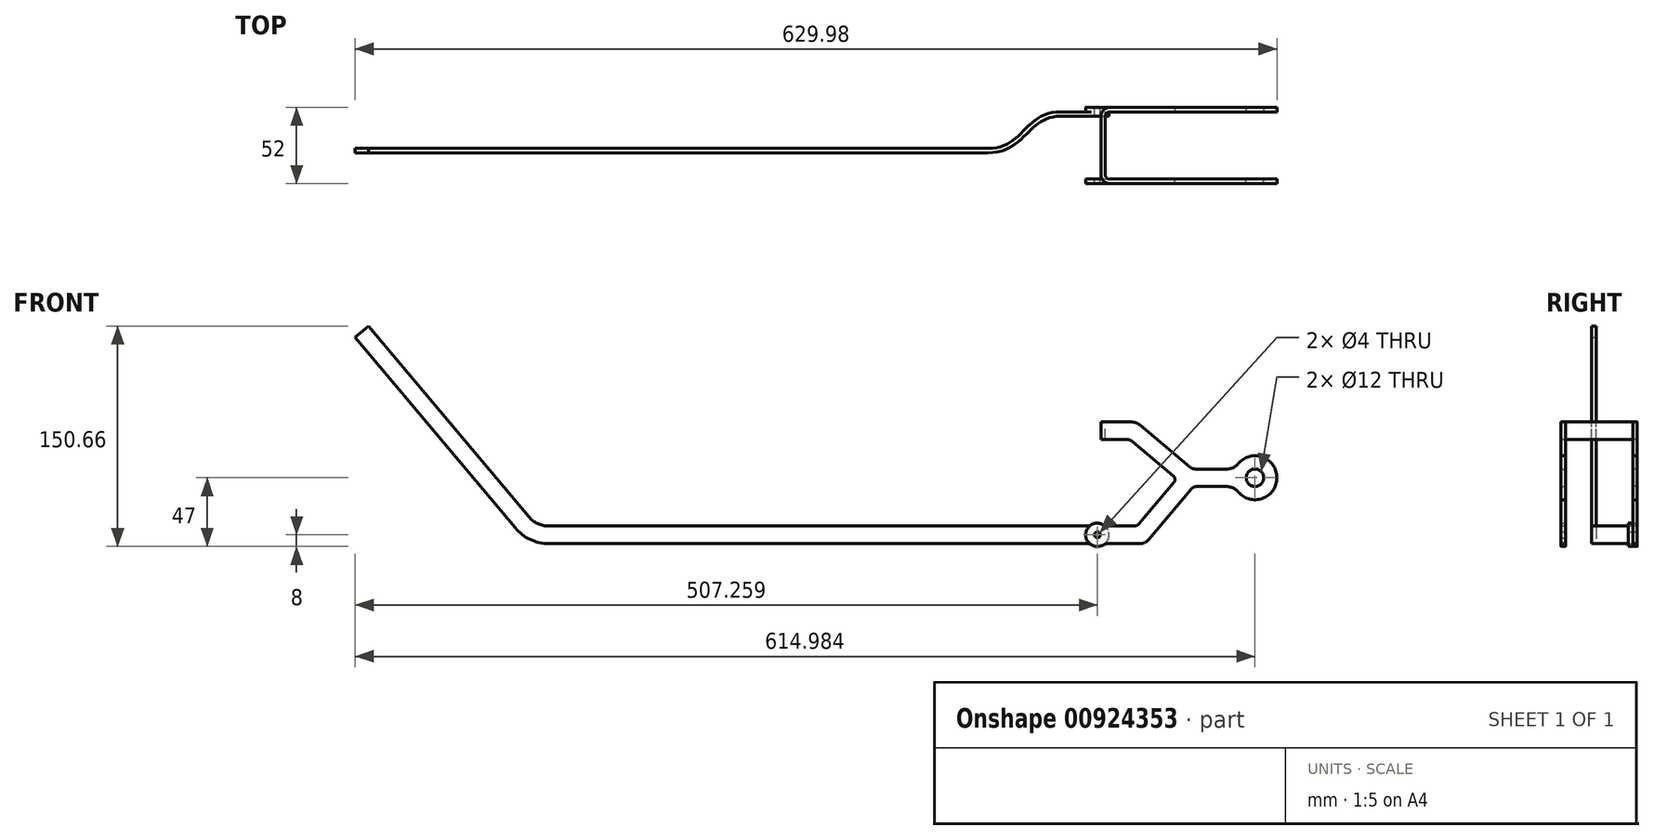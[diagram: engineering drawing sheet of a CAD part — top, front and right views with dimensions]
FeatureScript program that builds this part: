
annotation { "Feature Type Name" : "Feature", "Feature Type Description" : "" }
export const myFeature = defineFeature(function(context is Context, id is Id, definition is map)
    precondition{}
    {
        {
            var Q0;
            Q0=qCreatedBy(makeId("Front.planeOp"),FACE);
            var sketch = newSketch(context, id + "F0", { "sketchPlane" : qUnion([Q0])});
            skLineSegment(sketch, "E0", {"start": v(13.99, 0) * mm, "end": v(313.99, 0) * mm});
            skLineSegment(sketch, "E1", {"start": v(-9, 10.72) * mm, "end": v(-118.27, 140.94) * mm});
            skLineSegment(sketch, "E2", {"start": v(-23.81, 6) * mm, "end": v(-4.01, 6) * mm, "construction": true});
            skPoint(sketch, "E3.visualSharp", {"position": v(0, 0) * mm});
            skArc(sketch, "E3.filletArc", {"start": v(-9, 10.72) * mm, "mid": v(1.31, 2.81) * mm, "end": v(13.99, 0) * mm});
            skLineSegment(sketch, "E4.0", {"start": v(13.99, 12) * mm, "end": v(313.99, 12) * mm});
            skArc(sketch, "E4.1", {"start": v(0.2, 18.43) * mm, "mid": v(6.38, 13.69) * mm, "end": v(13.99, 12) * mm});
            skLineSegment(sketch, "E4.2", {"start": v(0.2, 18.43) * mm, "end": v(-109.07, 148.66) * mm});
            skLineSegment(sketch, "E5", {"start": v(-109.07, 148.66) * mm, "end": v(-118.27, 140.94) * mm});
            skLineSegment(sketch, "E6", {"start": v(313.99, 12) * mm, "end": v(313.99, 0) * mm});
            skSolve(sketch);
        }
        {
            var Q0;
            Q0=makeQuery(id+"F0.imprint","IMPRINT",FACE,{"disambiguationData":[TD([[makeQuery(id+"F0.imprint","IMPRINT",EDGE,{"derivedFrom":sQuery(id+"F0.wireOp",EDGE,"E0")}),1.0]])]});
            extrude(context, id + "F1", {"entities" : qUnion([Q0]), "depth" : 3 * mm, "offsetDistance" : 25 * mm});
        }
        {
            var Q0;
            Q0=qCreatedBy(makeId("Top.planeOp"),FACE);
            var sketch = newSketch(context, id + "F2", { "sketchPlane" : qUnion([Q0])});
            skLineSegment(sketch, "E7.0", {"start": v(13.99, 0) * mm, "end": v(313.99, 0) * mm});
            skSolve(sketch);
        }
        {
            var Q0;
            Q0=makeQuery(id+"F1.opExtrude","CAP_FACE",FACE,{"disambiguationData":[OSD([sQuery(id+"F0.wireOp",EDGE,"E0"),sQuery(id+"F0.wireOp",EDGE,"E1"),sQuery(id+"F0.wireOp",EDGE,"E3.filletArc"),sQuery(id+"F0.wireOp",EDGE,"E4.0"),sQuery(id+"F0.wireOp",EDGE,"E4.1"),sQuery(id+"F0.wireOp",EDGE,"E4.2"),sQuery(id+"F0.wireOp",EDGE,"E5"),sQuery(id+"F0.wireOp",EDGE,"E6")])],"isStart":true});
            cPlane(context, id + "F3", {"entities" : qUnion([Q0]), "cplaneType" : CPlaneType.OFFSET, "offset" : 25 * mm, "width" : 150 * mm, "height" : 150 * mm});
        }
        {
            var Q0;
            Q0=makeQuery(id+"F1.opExtrude","SWEPT_FACE",FACE,{"disambiguationData":[OSD([sQuery(id+"F0.wireOp",EDGE,"E0")])]});
            var sketch = newSketch(context, id + "F4", { "sketchPlane" : qUnion([Q0])});
            skPoint(sketch, "E8.0", {"position": v(313.99, 0) * mm});
            skFitSpline(sketch, "E9", {"points": [v(313.99, 0) * mm, v(363.99, -25) * mm], "startDerivative": vector(75, 0) * mm, "endDerivative": vector(75, 0) * mm});
            skLineSegment(sketch, "E10", {"start": v(363.99, -25) * mm, "end": v(388.99, -25) * mm});
            skLineSegment(sketch, "E11", {"start": v(363.99, -25) * mm, "end": v(241.15, -25) * mm, "construction": true});
            skSolve(sketch);
        }
        {
            var Q0;
            Q0=makeQuery(id+"F1.opExtrude","SWEPT_FACE",FACE,{"disambiguationData":[OSD([sQuery(id+"F0.wireOp",EDGE,"E6")])]});
            var Q1;
            Q1=sQuery(id+"F4.wireOp",EDGE,"E9");
            var Q2;
            Q2=sQuery(id+"F4.wireOp",EDGE,"E10");
            sweep(context, id + "F5", {"operationType" : NewBodyOperationType.ADD, "profiles" : qUnion([Q0]), "path" : qUnion([Q1, Q2])});
        }
        {
            var Q0;
            {var subQ0=sQuery(id+"F4.wireOp",EDGE,"E10");var subQ1=sQuery(id+"F0.wireOp",EDGE,"E6");Q0=makeQuery(id+"F5.opSweep","SWEPT_FACE",FACE,{"disambiguationData":[OSD([subQ1,subQ0]),TDD([makeQuery(id+"F1.opExtrude","CAP_EDGE",EDGE,{"disambiguationData":[OSD([subQ1])],"isStart":true}),subQ0])]});}
            var sketch = newSketch(context, id + "F6", { "sketchPlane" : qUnion([Q0])});
            skCircle(sketch, "E12", {"center": v(-388.99, 6) * mm, "radius": 6 * mm});
            skCircle(sketch, "E13", {"center": v(-388.99, 6) * mm, "radius": 2 * mm});
            skCircle(sketch, "E14", {"center": v(-388.99, 6) * mm, "radius": 8 * mm});
            skSolve(sketch);
        }
        {
            var Q0;
            {var subQ2=sQuery(id+"F0.wireOp",EDGE,"E6");var subQ4=sQuery(id+"F4.wireOp",EDGE,"E10");var subQ5=sQuery(id+"F0.wireOp",EDGE,"E0");var subQ6=makeQuery(id+"F5.opSweep","SWEPT_EDGE",EDGE,{"disambiguationData":[OSD([subQ5,subQ2,subQ4]),TDD([makeQuery(id+"F1.opExtrude","CAP_VERTEX",VERTEX,{"disambiguationData":[OSD([subQ5,subQ2])],"isStart":true}),subQ4])]});var subQ11=sQuery(id+"F6.wireOp",EDGE,"E14");var subQ13=makeQuery(id+"F6.imprint","INTERSECT",VERTEX,{"derivedFrom":[subQ6,subQ11]});Q0=makeQuery(id+"F6.imprint","IMPRINT",FACE,{"disambiguationData":[TD([[makeQuery(id+"F6.imprint","IMPRINT",EDGE,{"disambiguationData":[TD([[subQ13,1.0]])],"derivedFrom":subQ11}),1.0]])]});}
            var Q1;
            {var subQ1=sQuery(id+"F4.wireOp",VERTEX,"E10.end");var subQ2=sQuery(id+"F0.wireOp",EDGE,"E6");var subQ3=makeQuery(id+"F5.opSweep","CAP_EDGE",EDGE,{"disambiguationData":[OSD([subQ2,subQ1]),TDD([makeQuery(id+"F1.opExtrude","CAP_EDGE",EDGE,{"disambiguationData":[OSD([subQ2])],"isStart":true}),subQ1])],"isStart":false});var subQ9=sQuery(id+"F6.wireOp",EDGE,"E13");var subQ10=makeQuery(id+"F6.imprint","INTERSECT",VERTEX,{"disambiguationData":[OD(0.0)],"derivedFrom":[subQ3,subQ9]});Q1=makeQuery(id+"F6.imprint","IMPRINT",FACE,{"disambiguationData":[TD([[makeQuery(id+"F6.imprint","IMPRINT",EDGE,{"disambiguationData":[TD([[subQ10,1.0]])],"derivedFrom":subQ9}),-1.0]])]});}
            var Q2;
            {var subQ1=sQuery(id+"F4.wireOp",VERTEX,"E10.end");var subQ2=sQuery(id+"F0.wireOp",EDGE,"E6");var subQ3=makeQuery(id+"F5.opSweep","CAP_EDGE",EDGE,{"disambiguationData":[OSD([subQ2,subQ1]),TDD([makeQuery(id+"F1.opExtrude","CAP_EDGE",EDGE,{"disambiguationData":[OSD([subQ2])],"isStart":true}),subQ1])],"isStart":false});var subQ9=sQuery(id+"F6.wireOp",EDGE,"E13");var subQ10=makeQuery(id+"F6.imprint","INTERSECT",VERTEX,{"disambiguationData":[OD(0.0)],"derivedFrom":[subQ3,subQ9]});Q2=makeQuery(id+"F6.imprint","IMPRINT",FACE,{"disambiguationData":[TD([[makeQuery(id+"F6.imprint","IMPRINT",EDGE,{"disambiguationData":[TD([[subQ10,-1.0]])],"derivedFrom":subQ9}),-1.0]])]});}
            var Q3;
            {var subQ2=sQuery(id+"F0.wireOp",EDGE,"E6");var subQ4=sQuery(id+"F4.wireOp",EDGE,"E10");var subQ5=sQuery(id+"F0.wireOp",EDGE,"E0");var subQ6=makeQuery(id+"F5.opSweep","SWEPT_EDGE",EDGE,{"disambiguationData":[OSD([subQ5,subQ2,subQ4]),TDD([makeQuery(id+"F1.opExtrude","CAP_VERTEX",VERTEX,{"disambiguationData":[OSD([subQ5,subQ2])],"isStart":true}),subQ4])]});var subQ11=sQuery(id+"F6.wireOp",EDGE,"E14");var subQ12=makeQuery(id+"F6.imprint","INTERSECT",VERTEX,{"derivedFrom":[subQ6,subQ11]});Q3=makeQuery(id+"F6.imprint","IMPRINT",FACE,{"disambiguationData":[TD([[makeQuery(id+"F6.imprint","IMPRINT",EDGE,{"disambiguationData":[TD([[subQ12,-1.0]])],"derivedFrom":subQ11}),1.0]])]});}
            var Q4;
            {var subQ0=sQuery(id+"F6.wireOp",EDGE,"E13");var subQ1=sQuery(id+"F4.wireOp",VERTEX,"E10.end");var subQ2=sQuery(id+"F0.wireOp",EDGE,"E6");var subQ3=makeQuery(id+"F5.opSweep","CAP_EDGE",EDGE,{"disambiguationData":[OSD([subQ2,subQ1]),TDD([makeQuery(id+"F1.opExtrude","CAP_EDGE",EDGE,{"disambiguationData":[OSD([subQ2])],"isStart":true}),subQ1])],"isStart":false});var subQ4=makeQuery(id+"F6.imprint","INTERSECT",VERTEX,{"disambiguationData":[OD(0.0)],"derivedFrom":[subQ3,subQ0]});Q4=makeQuery(id+"F6.imprint","IMPRINT",FACE,{"disambiguationData":[TD([[makeQuery(id+"F6.imprint","IMPRINT",EDGE,{"disambiguationData":[TD([[subQ4,1.0]])],"derivedFrom":subQ0}),1.0]])]});}
            var Q5;
            {var subQ0=sQuery(id+"F6.wireOp",EDGE,"E13");var subQ1=sQuery(id+"F4.wireOp",VERTEX,"E10.end");var subQ2=sQuery(id+"F0.wireOp",EDGE,"E6");var subQ3=makeQuery(id+"F5.opSweep","CAP_EDGE",EDGE,{"disambiguationData":[OSD([subQ2,subQ1]),TDD([makeQuery(id+"F1.opExtrude","CAP_EDGE",EDGE,{"disambiguationData":[OSD([subQ2])],"isStart":true}),subQ1])],"isStart":false});var subQ4=makeQuery(id+"F6.imprint","INTERSECT",VERTEX,{"disambiguationData":[OD(0.0)],"derivedFrom":[subQ3,subQ0]});Q5=makeQuery(id+"F6.imprint","IMPRINT",FACE,{"disambiguationData":[TD([[makeQuery(id+"F6.imprint","IMPRINT",EDGE,{"disambiguationData":[TD([[subQ4,-1.0]])],"derivedFrom":subQ0}),1.0]])]});}
            extrude(context, id + "F7", {"entities" : qUnion([Q0, Q1, Q2, Q3, Q4, Q5]), "operationType" : NewBodyOperationType.ADD, "oppositeDirection" : true, "depth" : 3 * mm, "offsetDistance" : 25 * mm});
        }
        {
            var Q0;
            {var subQ0=sQuery(id+"F6.wireOp",EDGE,"E13");var subQ1=sQuery(id+"F4.wireOp",VERTEX,"E10.end");var subQ2=sQuery(id+"F0.wireOp",EDGE,"E6");var subQ3=makeQuery(id+"F5.opSweep","CAP_EDGE",EDGE,{"disambiguationData":[OSD([subQ2,subQ1]),TDD([makeQuery(id+"F1.opExtrude","CAP_EDGE",EDGE,{"disambiguationData":[OSD([subQ2])],"isStart":true}),subQ1])],"isStart":false});var subQ4=makeQuery(id+"F6.imprint","INTERSECT",VERTEX,{"disambiguationData":[OD(0.0)],"derivedFrom":[subQ3,subQ0]});Q0=makeQuery(id+"F6.imprint","IMPRINT",FACE,{"disambiguationData":[TD([[makeQuery(id+"F6.imprint","IMPRINT",EDGE,{"disambiguationData":[TD([[subQ4,1.0]])],"derivedFrom":subQ0}),1.0]])]});}
            var Q1;
            {var subQ0=sQuery(id+"F6.wireOp",EDGE,"E13");var subQ1=sQuery(id+"F4.wireOp",VERTEX,"E10.end");var subQ2=sQuery(id+"F0.wireOp",EDGE,"E6");var subQ3=makeQuery(id+"F5.opSweep","CAP_EDGE",EDGE,{"disambiguationData":[OSD([subQ2,subQ1]),TDD([makeQuery(id+"F1.opExtrude","CAP_EDGE",EDGE,{"disambiguationData":[OSD([subQ2])],"isStart":true}),subQ1])],"isStart":false});var subQ4=makeQuery(id+"F6.imprint","INTERSECT",VERTEX,{"disambiguationData":[OD(0.0)],"derivedFrom":[subQ3,subQ0]});Q1=makeQuery(id+"F6.imprint","IMPRINT",FACE,{"disambiguationData":[TD([[makeQuery(id+"F6.imprint","IMPRINT",EDGE,{"disambiguationData":[TD([[subQ4,-1.0]])],"derivedFrom":subQ0}),1.0]])]});}
            extrude(context, id + "F8", {"entities" : qUnion([Q0, Q1]), "operationType" : NewBodyOperationType.REMOVE, "oppositeDirection" : true, "depth" : 25 * mm, "offsetDistance" : 25 * mm});
        }
        {
            var Q0;
            {var subQ0=sQuery(id+"F0.wireOp",EDGE,"E4.0");Q0=makeQuery(id+"F7.boolean.opBoolean","INTERSECT",EDGE,{"derivedFrom":[makeQuery(id+"F5.boolean.opBoolean","MERGE",FACE,{"derivedFrom":[makeQuery(id+"F1.opExtrude","SWEPT_FACE",FACE,{"disambiguationData":[OSD([subQ0])]}),makeQuery(id+"F5.opSweep","SWEPT_FACE",FACE,{"disambiguationData":[OSD([subQ0,sQuery(id+"F0.wireOp",EDGE,"E6"),sQuery(id+"F4.wireOp",EDGE,"E9")])]})]}),makeQuery(id+"F7.opExtrude","SWEPT_FACE",FACE,{"disambiguationData":[OSD([sQuery(id+"F6.wireOp",EDGE,"E14")])]})]});}
            var Q1;
            {var subQ0=sQuery(id+"F0.wireOp",EDGE,"E0");Q1=makeQuery(id+"F7.boolean.opBoolean","INTERSECT",EDGE,{"derivedFrom":[makeQuery(id+"F5.boolean.opBoolean","MERGE",FACE,{"derivedFrom":[makeQuery(id+"F1.opExtrude","SWEPT_FACE",FACE,{"disambiguationData":[OSD([subQ0])]}),makeQuery(id+"F5.opSweep","SWEPT_FACE",FACE,{"disambiguationData":[OSD([subQ0,sQuery(id+"F0.wireOp",EDGE,"E6"),sQuery(id+"F4.wireOp",EDGE,"E9")])]})]}),makeQuery(id+"F7.opExtrude","SWEPT_FACE",FACE,{"disambiguationData":[OSD([sQuery(id+"F6.wireOp",EDGE,"E14")])]})]});}
            fillet(context, id + "F9", {"entities" : qUnion([Q0, Q1]), "radius" : 5 * mm, "tangentPropagation" : true, "allowEdgeOverflow" : false});
        }
        {
            var Q0;
            Q0=qCreatedBy(id+"F3.planeOp",FACE);
            var sketch = newSketch(context, id + "F10", { "sketchPlane" : qUnion([Q0])});
            skArc(sketch, "E15.0", {"start": v(-393.25, -0.77) * mm, "mid": v(-380.99, 6) * mm, "end": v(-393.25, 12.77) * mm});
            skPoint(sketch, "E16.orphan", {"position": v(-382.06, 12) * mm});
            skPoint(sketch, "E17.orphan", {"position": v(-388.99, 0) * mm});
            skPoint(sketch, "E18.orphan", {"position": v(-363.99, 12) * mm});
            skPoint(sketch, "E19.orphan", {"position": v(-363.99, 0) * mm});
            skLineSegment(sketch, "E20", {"start": v(-363.99, 0) * mm, "end": v(-363.99, -55) * mm, "construction": true});
            skLineSegment(sketch, "E21", {"start": v(-363.99, -55) * mm, "end": v(-590.7, -55) * mm, "construction": true});
            skCircle(sketch, "E22", {"center": v(-496.71, 45) * mm, "radius": 100 * mm});
            skArc(sketch, "E23", {"start": v(-485.19, 54.6) * mm, "mid": v(-511.71, 45) * mm, "end": v(-485.19, 35.4) * mm});
            skLineSegment(sketch, "E24", {"start": v(-388.99, 6) * mm, "end": v(-418.99, 6) * mm, "construction": true});
            skLineSegment(sketch, "E25", {"start": v(-418.99, 6) * mm, "end": v(-451.71, 45) * mm, "construction": true});
            skLineSegment(sketch, "E26", {"start": v(-451.71, 45) * mm, "end": v(-481.71, 45) * mm, "construction": true});
            skLineSegment(sketch, "E27.0", {"start": v(-455.72, 51) * mm, "end": v(-477.5, 51) * mm});
            skLineSegment(sketch, "E27.1", {"start": v(-417.7, 13.79) * mm, "end": v(-441.33, 41.96) * mm});
            skLineSegment(sketch, "E27.2", {"start": v(-395.92, 12) * mm, "end": v(-413.86, 12) * mm});
            skLineSegment(sketch, "E28.0", {"start": v(-456.84, 39) * mm, "end": v(-477.5, 39) * mm});
            skLineSegment(sketch, "E28.1", {"start": v(-424.18, 2.86) * mm, "end": v(-453.01, 37.21) * mm});
            skLineSegment(sketch, "E28.2", {"start": v(-395.92, 0) * mm, "end": v(-418.06, 0) * mm});
            skPoint(sketch, "E29.visualSharp", {"position": v(-482.97, 51) * mm});
            skArc(sketch, "E29.filletArc", {"start": v(-485.19, 54.6) * mm, "mid": v(-481.75, 51.94) * mm, "end": v(-477.5, 51) * mm});
            skPoint(sketch, "E30.visualSharp", {"position": v(-482.97, 39) * mm});
            skArc(sketch, "E30.filletArc", {"start": v(-477.5, 39) * mm, "mid": v(-481.75, 38.06) * mm, "end": v(-485.19, 35.4) * mm});
            skPoint(sketch, "E31.visualSharp", {"position": v(-454.51, 39) * mm});
            skArc(sketch, "E31.filletArc", {"start": v(-453.01, 37.21) * mm, "mid": v(-454.73, 38.53) * mm, "end": v(-456.84, 39) * mm});
            skPoint(sketch, "E32.visualSharp", {"position": v(-448.92, 51) * mm});
            skPoint(sketch, "E33.visualSharp", {"position": v(-416.2, 12) * mm});
            skArc(sketch, "E33.filletArc", {"start": v(-417.7, 13.79) * mm, "mid": v(-415.97, 12.47) * mm, "end": v(-413.86, 12) * mm});
            skPoint(sketch, "E34.visualSharp", {"position": v(-421.79, 0) * mm});
            skArc(sketch, "E34.filletArc", {"start": v(-424.18, 2.86) * mm, "mid": v(-421.44, 0.75) * mm, "end": v(-418.06, 0) * mm});
            skPoint(sketch, "E35.visualSharp", {"position": v(-394.28, 12) * mm});
            skArc(sketch, "E35.filletArc", {"start": v(-395.92, 12) * mm, "mid": v(-394.53, 12.2) * mm, "end": v(-393.25, 12.77) * mm});
            skPoint(sketch, "E36.visualSharp", {"position": v(-394.28, 0) * mm});
            skArc(sketch, "E36.filletArc", {"start": v(-393.25, -0.77) * mm, "mid": v(-394.53, -0.2) * mm, "end": v(-395.92, 0) * mm});
            skCircle(sketch, "E37", {"center": v(-496.71, 45) * mm, "radius": 6 * mm});
            skCircle(sketch, "E38.0", {"center": v(-388.99, 6) * mm, "radius": 2 * mm});
            skLineSegment(sketch, "E39", {"start": v(-451.71, 45) * mm, "end": v(-413.45, 77.1) * mm, "construction": true});
            skLineSegment(sketch, "E40.0", {"start": v(-452.5, 52.17) * mm, "end": v(-417.87, 81.23) * mm});
            skLineSegment(sketch, "E41.0", {"start": v(-440.96, 46.19) * mm, "end": v(-412.66, 69.94) * mm});
            skPoint(sketch, "E42.visualSharp", {"position": v(-453.9, 51) * mm});
            skArc(sketch, "E42.filletArc", {"start": v(-455.72, 51) * mm, "mid": v(-454, 51.3) * mm, "end": v(-452.5, 52.17) * mm});
            skPoint(sketch, "E43.visualSharp", {"position": v(-443.26, 44.26) * mm});
            skArc(sketch, "E43.filletArc", {"start": v(-440.96, 46.19) * mm, "mid": v(-442.02, 44.15) * mm, "end": v(-441.33, 41.96) * mm});
            skLineSegment(sketch, "E44", {"start": v(-413.45, 77.1) * mm, "end": v(-403.45, 77.1) * mm, "construction": true});
            skLineSegment(sketch, "E45.0", {"start": v(-409.45, 71.1) * mm, "end": v(-403.45, 71.1) * mm});
            skLineSegment(sketch, "E46.0", {"start": v(-412.72, 83.1) * mm, "end": v(-403.45, 83.1) * mm});
            skLineSegment(sketch, "E47", {"start": v(-403.45, 71.1) * mm, "end": v(-403.45, 83.1) * mm});
            skPoint(sketch, "E48.visualSharp", {"position": v(-415.64, 83.1) * mm});
            skArc(sketch, "E48.filletArc", {"start": v(-412.72, 83.1) * mm, "mid": v(-415.46, 82.62) * mm, "end": v(-417.87, 81.23) * mm});
            skPoint(sketch, "E49.visualSharp", {"position": v(-411.27, 71.1) * mm});
            skArc(sketch, "E49.filletArc", {"start": v(-409.45, 71.1) * mm, "mid": v(-411.16, 70.8) * mm, "end": v(-412.66, 69.94) * mm});
            skSolve(sketch);
        }
        {
            var Q0;
            Q0=makeQuery(id+"F10.imprint","IMPRINT",FACE,{"disambiguationData":[TD([[makeQuery(id+"F10.imprint","IMPRINT",EDGE,{"derivedFrom":sQuery(id+"F10.wireOp",EDGE,"E23")}),1.0]])]});
            var Q1;
            Q1=makeQuery(id+"F10.imprint","IMPRINT",FACE,{"disambiguationData":[TD([[makeQuery(id+"F10.imprint","IMPRINT",EDGE,{"derivedFrom":sQuery(id+"F10.wireOp",EDGE,"E15.0")}),1.0]])]});
            var Q2;
            {var subQ5=sQuery(id+"F10.wireOp",EDGE,"E47");Q2=makeQuery(id+"F10.imprint","IMPRINT",FACE,{"disambiguationData":[TD([[makeQuery(id+"F10.imprint","IMPRINT",EDGE,{"derivedFrom":subQ5}),1.0]])]});}
            extrude(context, id + "F11", {"entities" : qUnion([Q0, Q1, Q2]), "depth" : 3 * mm, "offsetDistance" : 25 * mm});
        }
        {
            var Q0;
            Q0=makeQuery(id+"F11.opExtrude","SWEPT_FACE",FACE,{"disambiguationData":[OSD([sQuery(id+"F10.wireOp",EDGE,"E46.0")])]});
            var sketch = newSketch(context, id + "F12", { "sketchPlane" : qUnion([Q0])});
            skLineSegment(sketch, "E50.0", {"start": v(412.72, 25) * mm, "end": v(403.45, 25) * mm});
            skLineSegment(sketch, "E51", {"start": v(403.45, 25) * mm, "end": v(397.45, 25) * mm});
            skLineSegment(sketch, "E52", {"start": v(394.45, 22) * mm, "end": v(394.45, -18) * mm});
            skPoint(sketch, "E53.visualSharp", {"position": v(394.45, 25) * mm});
            skArc(sketch, "E53.filletArc", {"start": v(397.45, 25) * mm, "mid": v(395.33, 24.12) * mm, "end": v(394.45, 22) * mm});
            skLineSegment(sketch, "E54", {"start": v(394.45, 2) * mm, "end": v(428.98, 2) * mm, "construction": true});
            skLineSegment(sketch, "E55.MirrorCS", {"start": v(403.45, -21) * mm, "end": v(397.45, -21) * mm});
            skArc(sketch, "E56.MirrorCS", {"start": v(397.45, -21) * mm, "mid": v(395.33, -20.12) * mm, "end": v(394.45, -18) * mm});
            skSolve(sketch);
        }
        {
            var Q0;
            Q0=makeQuery(id+"F11.opExtrude","SWEPT_FACE",FACE,{"disambiguationData":[OSD([sQuery(id+"F10.wireOp",EDGE,"E47")])]});
            var sketch = newSketch(context, id + "F13", { "sketchPlane" : qUnion([Q0])});
            skLineSegment(sketch, "E57.0.0", {"start": v(-25, 71.1) * mm, "end": v(-25, 83.1) * mm});
            skLineSegment(sketch, "E57.0.1", {"start": v(-25, 83.1) * mm, "end": v(-28, 83.1) * mm});
            skLineSegment(sketch, "E57.0.2", {"start": v(-28, 83.1) * mm, "end": v(-28, 71.1) * mm});
            skLineSegment(sketch, "E57.0.3", {"start": v(-28, 71.1) * mm, "end": v(-25, 71.1) * mm});
            skSolve(sketch);
        }
        {
            var Q0;
            Q0=makeQuery(id+"F13.imprint","IMPRINT",FACE,{"disambiguationData":[TD([[makeQuery(id+"F13.imprint","IMPRINT",EDGE,{"derivedFrom":sQuery(id+"F13.wireOp",EDGE,"E57.0.0")}),1.0]])]});
            var Q1;
            Q1=sQuery(id+"F12.wireOp",EDGE,"E51");
            var Q2;
            Q2=sQuery(id+"F12.wireOp",EDGE,"E53.filletArc");
            var Q3;
            Q3=sQuery(id+"F12.wireOp",EDGE,"E52");
            var Q4;
            Q4=sQuery(id+"F12.wireOp",EDGE,"E56.MirrorCS");
            var Q5;
            Q5=sQuery(id+"F12.wireOp",EDGE,"E55.MirrorCS");
            sweep(context, id + "F14", {"operationType" : NewBodyOperationType.ADD, "profiles" : qUnion([Q0]), "path" : qUnion([Q1, Q2, Q3, Q4, Q5])});
        }
        {
            var Q0;
            Q0=sQuery(id+"F12.wireOp",EDGE,"E54");
            cPlane(context, id + "F15", {"entities" : qUnion([Q0]), "cplaneType" : CPlaneType.LINE_ANGLE, "offset" : 25 * mm, "angle" : 0 * degree, "width" : 150 * mm, "height" : 150 * mm});
        }
        {
            var Q0;
            Q0=makeQuery(id+"F11.opExtrude","SWEPT_BODY",BODY,{"disambiguationData":[OSD([sQuery(id+"F10.wireOp",EDGE,"E15.0"),sQuery(id+"F10.wireOp",EDGE,"E23"),sQuery(id+"F10.wireOp",EDGE,"E27.0"),sQuery(id+"F10.wireOp",EDGE,"E27.1"),sQuery(id+"F10.wireOp",EDGE,"E27.2"),sQuery(id+"F10.wireOp",EDGE,"E28.0"),sQuery(id+"F10.wireOp",EDGE,"E28.1"),sQuery(id+"F10.wireOp",EDGE,"E28.2"),sQuery(id+"F10.wireOp",EDGE,"E29.filletArc"),sQuery(id+"F10.wireOp",EDGE,"E30.filletArc"),sQuery(id+"F10.wireOp",EDGE,"E31.filletArc"),sQuery(id+"F10.wireOp",EDGE,"E33.filletArc"),sQuery(id+"F10.wireOp",EDGE,"E34.filletArc"),sQuery(id+"F10.wireOp",EDGE,"E35.filletArc"),sQuery(id+"F10.wireOp",EDGE,"E36.filletArc"),sQuery(id+"F10.wireOp",EDGE,"E37"),sQuery(id+"F10.wireOp",EDGE,"E38.0"),sQuery(id+"F10.wireOp",EDGE,"E40.0"),sQuery(id+"F10.wireOp",EDGE,"E41.0"),sQuery(id+"F10.wireOp",EDGE,"E42.filletArc"),sQuery(id+"F10.wireOp",EDGE,"E43.filletArc"),sQuery(id+"F10.wireOp",EDGE,"E45.0"),sQuery(id+"F10.wireOp",EDGE,"E46.0"),sQuery(id+"F10.wireOp",EDGE,"E47"),sQuery(id+"F10.wireOp",EDGE,"E48.filletArc"),sQuery(id+"F10.wireOp",EDGE,"E49.filletArc")])]});
            var Q1;
            Q1=qCreatedBy(id+"F15.planeOp",FACE);
            mirror(context, id + "F16", {"operationType" : NewBodyOperationType.ADD, "entities" : qUnion([Q0]), "mirrorPlane" : qUnion([Q1])});
        }
    });
